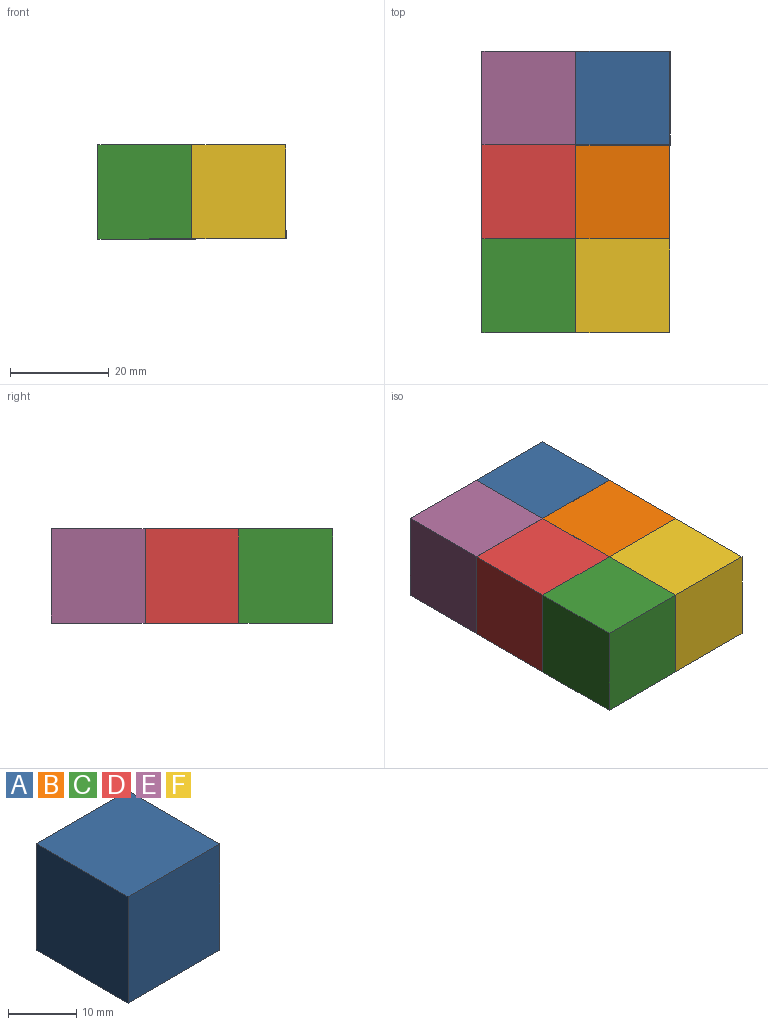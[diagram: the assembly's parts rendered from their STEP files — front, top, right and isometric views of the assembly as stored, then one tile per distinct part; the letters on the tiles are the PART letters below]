
ASSEMBLY  parts=6 mates=5
PART A: 6 faces, bbox 19.1x19.1x19.1 mm
  f0: plane 19.05x19.05mm, normal (0,0,1), area 362.9mm2, adj f1,f3,f4,f5
  f1: plane 19.1x19.05mm, normal (-1,0,0), area 363.9mm2, adj f0,f2,f4,f5
  f2: plane 19.05x19.05mm, normal (0,0,-1), area 362.9mm2, adj f1,f3,f4,f5
  f3: plane 19.05x19.05mm, normal (1,0,0), area 362.9mm2, adj f0,f2,f4,f5
  f4: plane 19.1x19.05mm, normal (0,-1,0), area 363.4mm2, adj f0,f1,f2,f3
  f5: plane 19.1x19.05mm, normal (0,1,0), area 363.4mm2, adj f0,f1,f2,f3
PART B: same geometry as A
PART C: same geometry as A
PART D: same geometry as A
PART E: same geometry as A
PART F: same geometry as A
PLACE A rot(axis=(0,-1,0),90.2deg) t=(-22.78,-7.93,9.89)mm
PLACE B rot(axis=(-0.58,-0.58,-0.58),120deg) t=(-13.48,-36.72,9.9)mm
PLACE C rot(axis=(1,0,0),180deg) t=(-42.41,-65.08,10.44)mm
PLACE D rot(axis=(1,0,0),180deg) t=(-42.41,-46.03,10.44)mm
PLACE E t=(-42.41,-7.93,10.02)mm fixed
PLACE F rot(axis=(-0.58,-0.58,-0.58),120deg) t=(-13.48,-55.77,9.9)mm
MATE fastened E.f4 <-> D.f4  axis (0,-1,0) through (-42.06,-26.98,10.23)mm
MATE fastened C.f3 <-> F.f4  axis (1,0,0) through (-32.53,-55.55,10.24)mm
MATE fastened D.f3 <-> B.f4  axis (1,0,0) through (-32.53,-36.5,10.24)mm
MATE fastened D.f5 <-> C.f4  axis (0,-1,0) through (-42.06,-46.03,10.23)mm
MATE fastened E.f3 <-> A.f0  axis (1,0,0) through (-32.53,-17.45,10.22)mm
